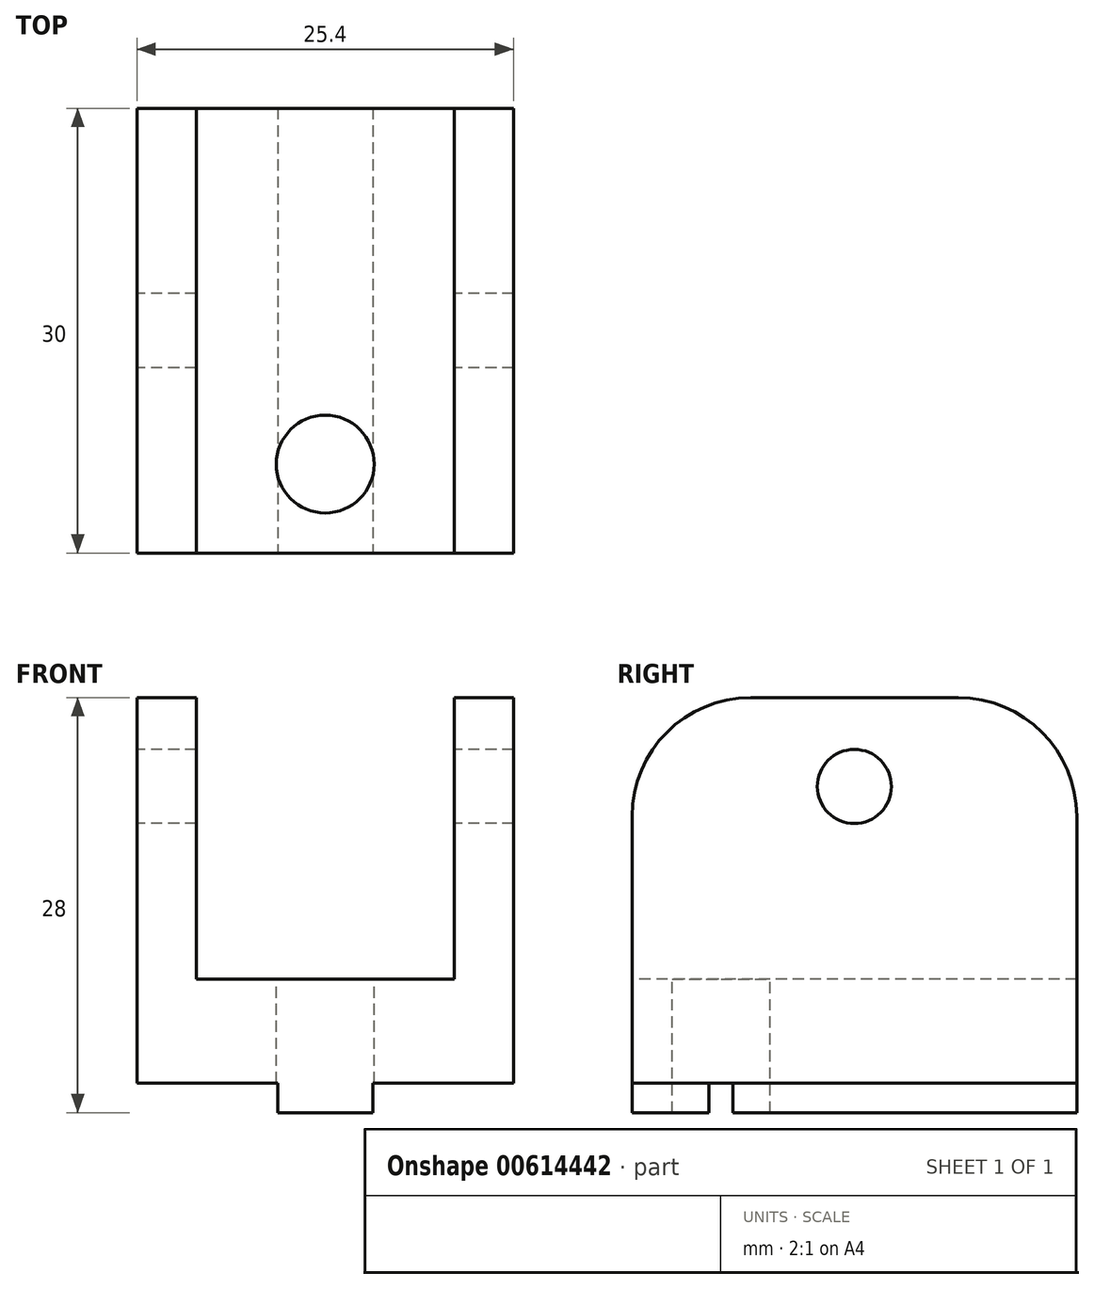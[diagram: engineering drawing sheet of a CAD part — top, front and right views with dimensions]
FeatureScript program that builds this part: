
annotation { "Feature Type Name" : "Feature", "Feature Type Description" : "" }
export const myFeature = defineFeature(function(context is Context, id is Id, definition is map)
    precondition{}
    {
        {
            var Q0;
            Q0=qCreatedBy(makeId("Right.planeOp"),FACE);
            var sketch = newSketch(context, id + "F0", { "sketchPlane" : qUnion([Q0])});
            skLineSegment(sketch, "E0.bottom", {"start": v(-7, 26) * mm, "end": v(7, 26) * mm});
            skLineSegment(sketch, "E0.top", {"start": v(-15, 0) * mm, "end": v(15, 0) * mm});
            skLineSegment(sketch, "E0.left", {"start": v(-15, 18) * mm, "end": v(-15, 0) * mm});
            skLineSegment(sketch, "E0.right", {"start": v(15, 18) * mm, "end": v(15, 0) * mm});
            skCircle(sketch, "E1", {"center": v(0, 20) * mm, "radius": 2.5 * mm});
            skPoint(sketch, "E2.visualSharp", {"position": v(-15, 26) * mm});
            skArc(sketch, "E2.filletArc", {"start": v(-7, 26) * mm, "mid": v(-12.66, 23.66) * mm, "end": v(-15, 18) * mm});
            skPoint(sketch, "E3.visualSharp", {"position": v(15, 26) * mm});
            skArc(sketch, "E3.filletArc", {"start": v(15, 18) * mm, "mid": v(12.66, 23.66) * mm, "end": v(7, 26) * mm});
            skSolve(sketch);
        }
        {
            var Q0;
            Q0 = qSketchRegion(id + "F0", true);
            extrude(context, id + "F1", {"entities" : qUnion([Q0]), "depth" : 25.4 * mm, "offsetDistance" : 25 * mm});
        }
        {
            var Q0;
            Q0=makeQuery(id+"F1.opExtrude","SWEPT_FACE",FACE,{"disambiguationData":[OSD([sQuery(id+"F0.wireOp",EDGE,"E0.bottom")])]});
            var sketch = newSketch(context, id + "F2", { "sketchPlane" : qUnion([Q0])});
            skLineSegment(sketch, "E4.bottom", {"start": v(4, 18.9) * mm, "end": v(21.4, 18.9) * mm});
            skLineSegment(sketch, "E4.top", {"start": v(4, -19.7) * mm, "end": v(21.4, -19.7) * mm});
            skLineSegment(sketch, "E4.left", {"start": v(4, 18.9) * mm, "end": v(4, -19.7) * mm});
            skLineSegment(sketch, "E4.right", {"start": v(21.4, 18.9) * mm, "end": v(21.4, -19.7) * mm});
            skSolve(sketch);
        }
        {
            var Q0;
            Q0 = qSketchRegion(id + "F2", true);
            extrude(context, id + "F3", {"entities" : qUnion([Q0]), "operationType" : NewBodyOperationType.REMOVE, "oppositeDirection" : true, "depth" : 19 * mm, "offsetDistance" : 25 * mm});
        }
        {
            var Q0;
            Q0=makeQuery(id+"F1.opExtrude","SWEPT_FACE",FACE,{"disambiguationData":[OSD([sQuery(id+"F0.wireOp",EDGE,"E0.top")])]});
            var sketch = newSketch(context, id + "F4", { "sketchPlane" : qUnion([Q0])});
            skLineSegment(sketch, "E5.bottom", {"start": v(15.9, -15) * mm, "end": v(9.5, -15) * mm});
            skLineSegment(sketch, "E5.top", {"start": v(15.9, 15) * mm, "end": v(9.5, 15) * mm});
            skLineSegment(sketch, "E5.left", {"start": v(15.9, -15) * mm, "end": v(15.9, 15) * mm});
            skLineSegment(sketch, "E5.right", {"start": v(9.5, -15) * mm, "end": v(9.5, 15) * mm});
            skLineSegment(sketch, "E6", {"start": v(12.7, -15) * mm, "end": v(12.7, 15) * mm, "construction": true});
            skLineSegment(sketch, "E7", {"start": v(12.7, 15) * mm, "end": v(13.72, 14.46) * mm, "construction": true});
            skSolve(sketch);
        }
        {
            var Q0;
            Q0 = qSketchRegion(id + "F4", true);
            extrude(context, id + "F5", {"entities" : qUnion([Q0]), "operationType" : NewBodyOperationType.ADD, "depth" : 2 * mm, "offsetDistance" : 25 * mm});
        }
        {
            var Q0;
            Q0=makeQuery(id+"F3.boolean.opBoolean","COPY",FACE,{"derivedFrom":makeQuery(id+"F3.opExtrude","CAP_FACE",FACE,{"disambiguationData":[OSD([sQuery(id+"F2.wireOp",EDGE,"E4.bottom"),sQuery(id+"F2.wireOp",EDGE,"E4.top"),sQuery(id+"F2.wireOp",EDGE,"E4.left"),sQuery(id+"F2.wireOp",EDGE,"E4.right")])],"isStart":false})});
            var sketch = newSketch(context, id + "F6", { "sketchPlane" : qUnion([Q0])});
            skCircle(sketch, "E8", {"center": v(12.7, -9) * mm, "radius": 3.3 * mm});
            skSolve(sketch);
        }
        {
            var Q0;
            Q0 = qSketchRegion(id + "F6", true);
            extrude(context, id + "F7", {"entities" : qUnion([Q0]), "operationType" : NewBodyOperationType.REMOVE, "oppositeDirection" : true, "depth" : 10 * mm, "offsetDistance" : 25 * mm});
        }
    });
